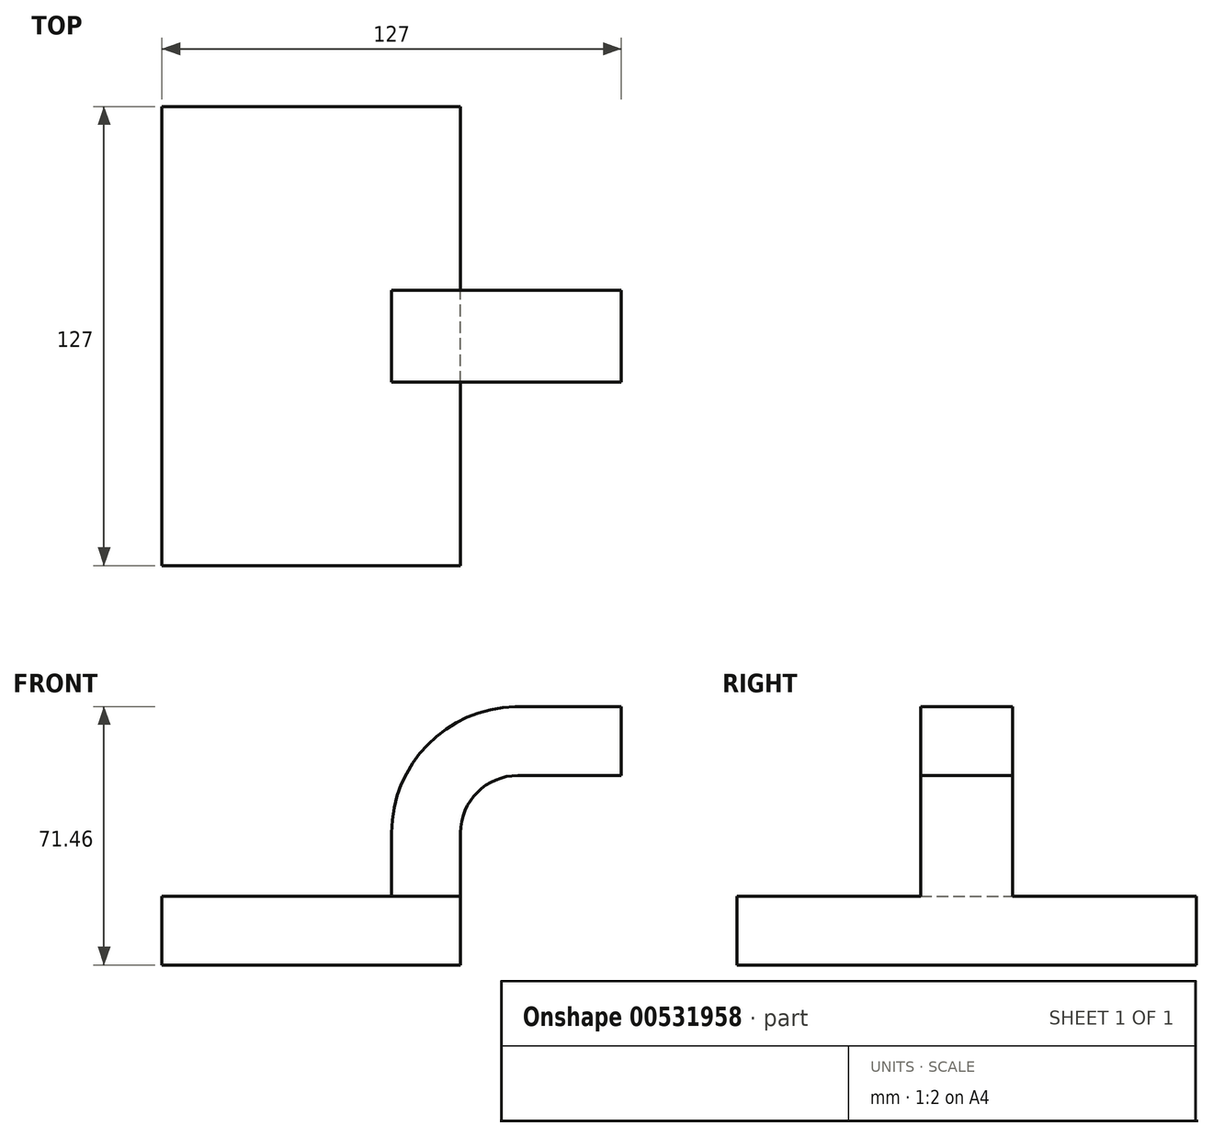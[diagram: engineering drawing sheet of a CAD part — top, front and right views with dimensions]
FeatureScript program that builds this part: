
annotation { "Feature Type Name" : "Feature", "Feature Type Description" : "" }
export const myFeature = defineFeature(function(context is Context, id is Id, definition is map)
    precondition{}
    {
        {
            var Q0;
            Q0=qCreatedBy(makeId("Front.planeOp"),FACE);
            var sketch = newSketch(context, id + "F0", { "sketchPlane" : qUnion([Q0])});
            skLineSegment(sketch, "E0.bottom", {"start": v(41.28, -9.52) * mm, "end": v(-41.28, -9.53) * mm});
            skLineSegment(sketch, "E0.top", {"start": v(41.28, 9.53) * mm, "end": v(-41.28, 9.53) * mm});
            skLineSegment(sketch, "E0.left", {"start": v(41.28, -9.52) * mm, "end": v(41.28, 9.53) * mm});
            skLineSegment(sketch, "E0.right", {"start": v(-41.28, -9.53) * mm, "end": v(-41.28, 9.53) * mm});
            skPoint(sketch, "E0.middle", {"position": v(0, 0) * mm});
            skLineSegment(sketch, "E1", {"start": v(41.28, 9.53) * mm, "end": v(41.28, 27) * mm});
            skArc(sketch, "E2", {"start": v(41.27, 27) * mm, "mid": v(45.92, 38.23) * mm, "end": v(57.15, 42.88) * mm});
            skLineSegment(sketch, "E3", {"start": v(57.15, 42.88) * mm, "end": v(85.73, 42.88) * mm});
            skLineSegment(sketch, "E4.0", {"start": v(57.15, 61.93) * mm, "end": v(85.73, 61.93) * mm});
            skArc(sketch, "E4.1", {"start": v(22.23, 27) * mm, "mid": v(32.45, 51.7) * mm, "end": v(57.15, 61.93) * mm});
            skLineSegment(sketch, "E4.2", {"start": v(22.22, 9.53) * mm, "end": v(22.22, 27) * mm});
            skLineSegment(sketch, "E5.bottom", {"start": v(111.12, 38.1) * mm, "end": v(60.33, 38.1) * mm});
            skLineSegment(sketch, "E5.top", {"start": v(111.12, 66.68) * mm, "end": v(60.33, 66.68) * mm});
            skLineSegment(sketch, "E5.left", {"start": v(111.12, 38.1) * mm, "end": v(111.12, 66.68) * mm});
            skLineSegment(sketch, "E5.right", {"start": v(60.33, 38.1) * mm, "end": v(60.33, 66.68) * mm});
            skPoint(sketch, "E5.middle", {"position": v(85.72, 52.39) * mm});
            skLineSegment(sketch, "E6", {"start": v(85.72, 38.1) * mm, "end": v(85.72, 66.68) * mm});
            skFitSpline(sketch, "E7", {"points": [v(-41.28, 9.53) * mm, v(57.15, 61.93) * mm], "startDerivative": vector(19.56, 72.25) * mm, "endDerivative": vector(137.7, 1.02) * mm});
            skSolve(sketch);
        }
        {
            var Q0;
            Q0=makeQuery(id+"F0.imprint","IMPRINT",FACE,{"disambiguationData":[TD([[makeQuery(id+"F0.imprint","IMPRINT",EDGE,{"derivedFrom":sQuery(id+"F0.wireOp",EDGE,"E0.bottom")}),-1.0]])]});
            extrude(context, id + "F1", {"entities" : qUnion([Q0]), "endBound" : BoundingType.SYMMETRIC, "depth" : 127 * mm, "offsetDistance" : 25.4 * mm});
        }
        {
            var Q0;
            {var subQ4=sQuery(id+"F0.wireOp",EDGE,"E1");Q0=makeQuery(id+"F0.imprint","IMPRINT",FACE,{"disambiguationData":[TD([[makeQuery(id+"F0.imprint","IMPRINT",EDGE,{"derivedFrom":subQ4}),1.0]])]});}
            var Q1;
            {var subQ0=sQuery(id+"F0.wireOp",EDGE,"E6");var subQ1=sQuery(id+"F0.wireOp",EDGE,"E3");var subQ2=makeQuery(id+"F0.imprint","INTERSECT",VERTEX,{"derivedFrom":[subQ1,subQ0]});Q1=makeQuery(id+"F0.imprint","IMPRINT",FACE,{"disambiguationData":[TD([[makeQuery(id+"F0.imprint","IMPRINT",EDGE,{"disambiguationData":[TD([[subQ2,1.0]])],"derivedFrom":subQ1}),1.0]])]});}
            extrude(context, id + "F2", {"entities" : qUnion([Q0, Q1]), "operationType" : NewBodyOperationType.ADD, "endBound" : BoundingType.SYMMETRIC, "depth" : 25.4 * mm, "offsetDistance" : 25.4 * mm});
        }
    });
